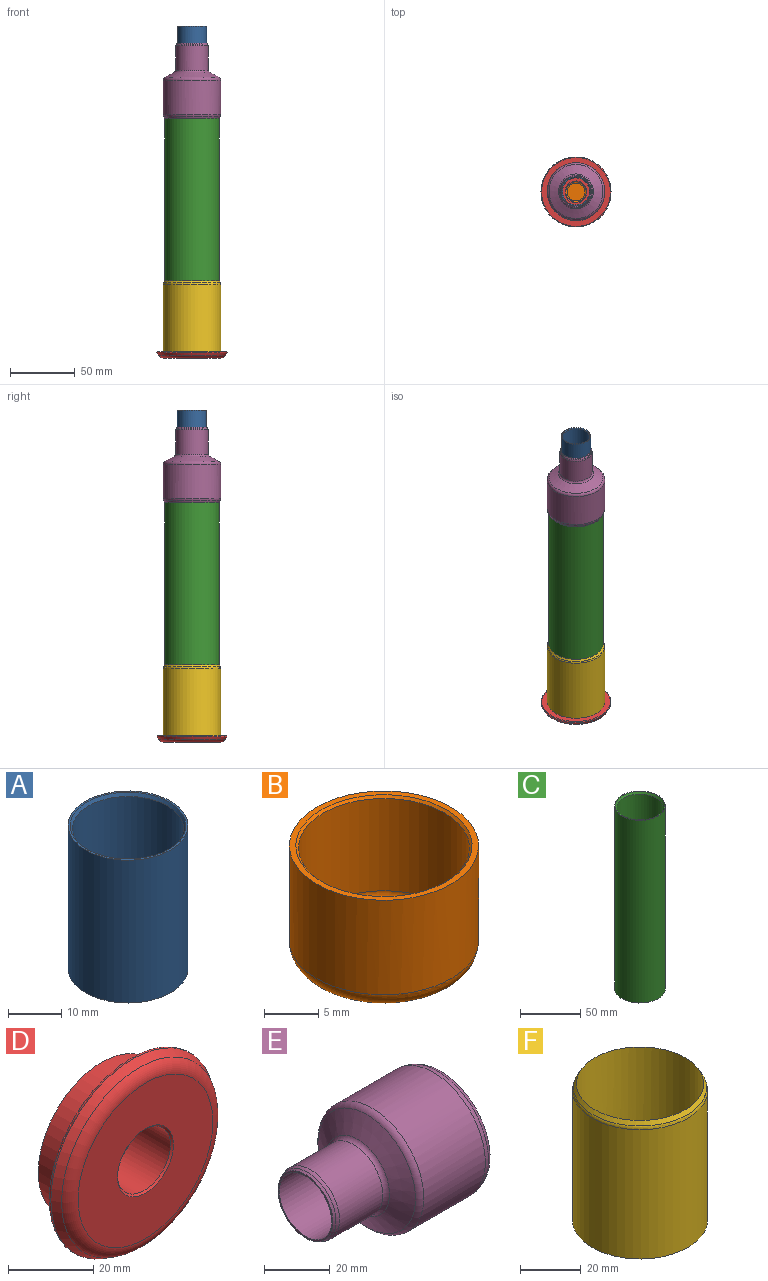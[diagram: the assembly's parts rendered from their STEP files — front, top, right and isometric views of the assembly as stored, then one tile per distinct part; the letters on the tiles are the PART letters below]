
ASSEMBLY  parts=6 mates=5
PART A: 6 faces, bbox 22.5x22.5x32.8 mm
  f0: cylinder r=10.45mm len=31.4mm, axis (0,0,-1), area 2061.7mm2, adj f4,f5
  f1: cylinder r=11.25mm len=32.8mm, axis (0,0,-1), area 2318.5mm2, adj f2,f3
  f2: plane 22.5x22.5mm, normal (0,0,1), area 27.5mm2, adj f1,f5
  f3: plane 22.5x22.5mm, normal (0,0,-1), area 27.5mm2, adj f1,f4
  f4: cone r=10.85mm half-angle=30deg, axis (0,0,-1), area 54.1mm2, adj f0,f3
  f5: cone r=10.45mm half-angle=30deg, axis (0,0,1), area 54.1mm2, adj f0,f2
PART B: 8 faces, bbox 18.9x18.9x12.5 mm
  f0: plane 13.9x13.9mm, normal (0,0,-1), area 151.7mm2, adj f3
  f1: cylinder r=8.75mm len=17.5mm, axis (0,0,-1), area 588.3mm2, adj f2,f3
  f2: plane 17.5x17.5mm, normal (0,0,1), area 31.9mm2, adj f1,f7
  f3: torus R=6.95mm, axis (0,0,1), area 143.8mm2, adj f0,f1
  f4: plane 13.9x13.9mm, normal (0,0,1), area 151.7mm2, adj f6
  f5: cylinder r=7.9mm len=15.8mm, axis (0,0,-1), area 518.7mm2, adj f6,f7
  f6: torus R=6.95mm, axis (0,0,1), area 70.8mm2, adj f4,f5
  f7: cone r=8.15mm half-angle=45deg, axis (0,0,1), area 17.8mm2, adj f2,f5
PART C: 6 faces, bbox 42x42x185 mm
  f0: plane 42x42mm, normal (0,0,-1), area 77.4mm2, adj f1,f4
  f1: cylinder r=21mm len=185mm, axis (0,0,-1), area 24410.2mm2, adj f0,f2
  f2: plane 42x42mm, normal (0,0,1), area 77.4mm2, adj f1,f5
  f3: cylinder r=19.25mm len=181mm, axis (0,0,1), area 21892.2mm2, adj f4,f5
  f4: cone r=20.4mm half-angle=30deg, axis (0,0,-1), area 287.7mm2, adj f0,f3
  f5: cone r=19.25mm half-angle=30deg, axis (0,0,1), area 287.7mm2, adj f2,f3
PART D: 13 faces, bbox 58.7x14.5x58.7 mm
  f0: cylinder r=21mm len=42mm, axis (0,1,0), area 1253.5mm2, adj f1,f4
  f1: plane 42x42mm, normal (0,1,0), area 1158.5mm2, adj f0,f10
  f2: plane 44.61x44.61mm, normal (0,-1,0), area 1294mm2, adj f5,f11
  f3: cone r=27.5mm half-angle=30deg, axis (0,1,0), area 431.2mm2, adj f5,f12
  f4: plane 53.27x53.27mm, normal (0,1,0), area 843.1mm2, adj f0,f12
  f5: torus R=22.3mm, axis (0,1,0), area 637.3mm2, adj f2,f3
  f6: cylinder r=8.75mm len=17.5mm, axis (0,-1,0), area 659.7mm2, adj f7,f11
  f7: plane 17.5x17.5mm, normal (0,-1,0), area 24.1mm2, adj f6,f9
  f8: cylinder r=8mm len=16mm, axis (0,1,0), area 60.3mm2, adj f9,f10
  f9: cone r=8mm half-angle=45deg, axis (0,-1,0), area 21.7mm2, adj f7,f8
  f10: torus R=8.5mm, axis (0,1,0), area 40.4mm2, adj f1,f8
  f11: cone r=8.75mm half-angle=45deg, axis (0,-1,0), area 40mm2, adj f2,f6
  f12: torus R=26.63mm, axis (0,1,0), area 177.6mm2, adj f3,f4
PART E: 16 faces, bbox 58.1x48.2x48.2 mm
  f0: plane 42.5x42.5mm, normal (1,0,0), area 33.2mm2, adj f7,f12
  f1: cylinder r=22.25mm len=44.5mm, axis (1,0,0), area 3698.3mm2, adj f5,f13
  f2: cone r=22.25mm half-angle=62.4deg, axis (1,0,0), area 896.3mm2, adj f5,f6
  f3: cylinder r=12.5mm len=25mm, axis (1,0,0), area 1462.7mm2, adj f6,f15
  f4: plane 23.6x23.6mm, normal (-1,0,0), area 39.9mm2, adj f9,f14
  f5: torus R=19.75mm, axis (-1,0,0), area 372.8mm2, adj f1,f2
  f6: torus R=14.5mm, axis (1,0,0), area 176.2mm2, adj f2,f3
  f7: cylinder r=21mm len=42mm, axis (1,0,0), area 3890.5mm2, adj f0,f10
  f8: cone r=21.67mm half-angle=62.4deg, axis (1,0,0), area 866.2mm2, adj f10,f11
  f9: cylinder r=11.25mm len=22.5mm, axis (1,0,0), area 1469.4mm2, adj f4,f11
  f10: torus R=19.75mm, axis (-1,0,0), area 177.7mm2, adj f7,f8
  f11: torus R=14.5mm, axis (1,0,0), area 263.8mm2, adj f8,f9
  f12: cone r=21.25mm half-angle=25deg, axis (-1,0,0), area 200.4mm2, adj f0,f13
  f13: torus R=18.25mm, axis (1,0,0), area 242.6mm2, adj f1,f12
  f14: cone r=12.5mm half-angle=25deg, axis (1,0,0), area 74.7mm2, adj f4,f15
  f15: torus R=9.5mm, axis (-1,0,0), area 102mm2, adj f3,f14
PART F: 5 faces, bbox 48.2x48.2x55 mm
  f0: cylinder r=21mm len=55mm, axis (0,0,-1), area 7257.1mm2, adj f2,f3
  f1: cylinder r=22.25mm len=52.17mm, axis (0,0,-1), area 7292.7mm2, adj f2,f4
  f2: plane 44.5x44.5mm, normal (0,0,-1), area 169.8mm2, adj f0,f1
  f3: cone r=21mm half-angle=30deg, axis (0,0,-1), area 246.7mm2, adj f0,f4
  f4: torus R=19.75mm, axis (0,0,1), area 182.1mm2, adj f1,f3
PLACE A t=(7.04,0,9.54)mm
PLACE B t=(11.41,0,-208.58)mm
PLACE C t=(17.54,0,-91.83)mm
PLACE D rot(axis=(1,0,0),90deg) t=(7.04,0,-200.33)mm
PLACE E rot(axis=(0,1,0),90deg) t=(7.06,0,7.02)mm fixed
PLACE F t=(7.04,0,-209.83)mm
MATE fastened C.f1 <-> E.f1  axis (0,0,1) through (7.04,0,-1.33)mm
MATE fastened B.f7 <-> D.f11  axis (0,0,-1) through (7.04,0,-214.83)mm
MATE fastened C.f1 <-> F.f0  axis (0,0,1) through (7.04,0,-182.33)mm
MATE fastened A.f0 <-> E.f1  axis (0,0,-1) through (7.04,0,10.24)mm
MATE fastened F.f0 <-> D.f0  axis (0,0,-1) through (7.04,0,-209.83)mm
